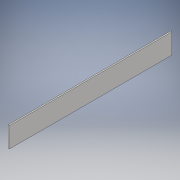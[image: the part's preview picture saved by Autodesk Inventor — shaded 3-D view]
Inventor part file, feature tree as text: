
AUTODESK INVENTOR PART (.ipt)
format: ipt  version: 2017 (Build 210142000, 142)  size: 90,624 bytes
history: native  units: in
note: dims shown in document units (in); Inventor stores cm internally (conversion verified against a paired STEP export)
features: extrude x1, sketch x1
ambient origin geometry x8: Origin, YZ Plane, XZ Plane, XY Plane, X Axis, Y Axis, Z Axis, Center Point
bodies: Solid1 (feature_tree)
feature tree (2):
  extrude  "Extrusion1"  Depth=2.0in
  sketch  "Sketch1"  dims[d0=0.125in d1=2.0in d2=16.0in d3=0.0in]
